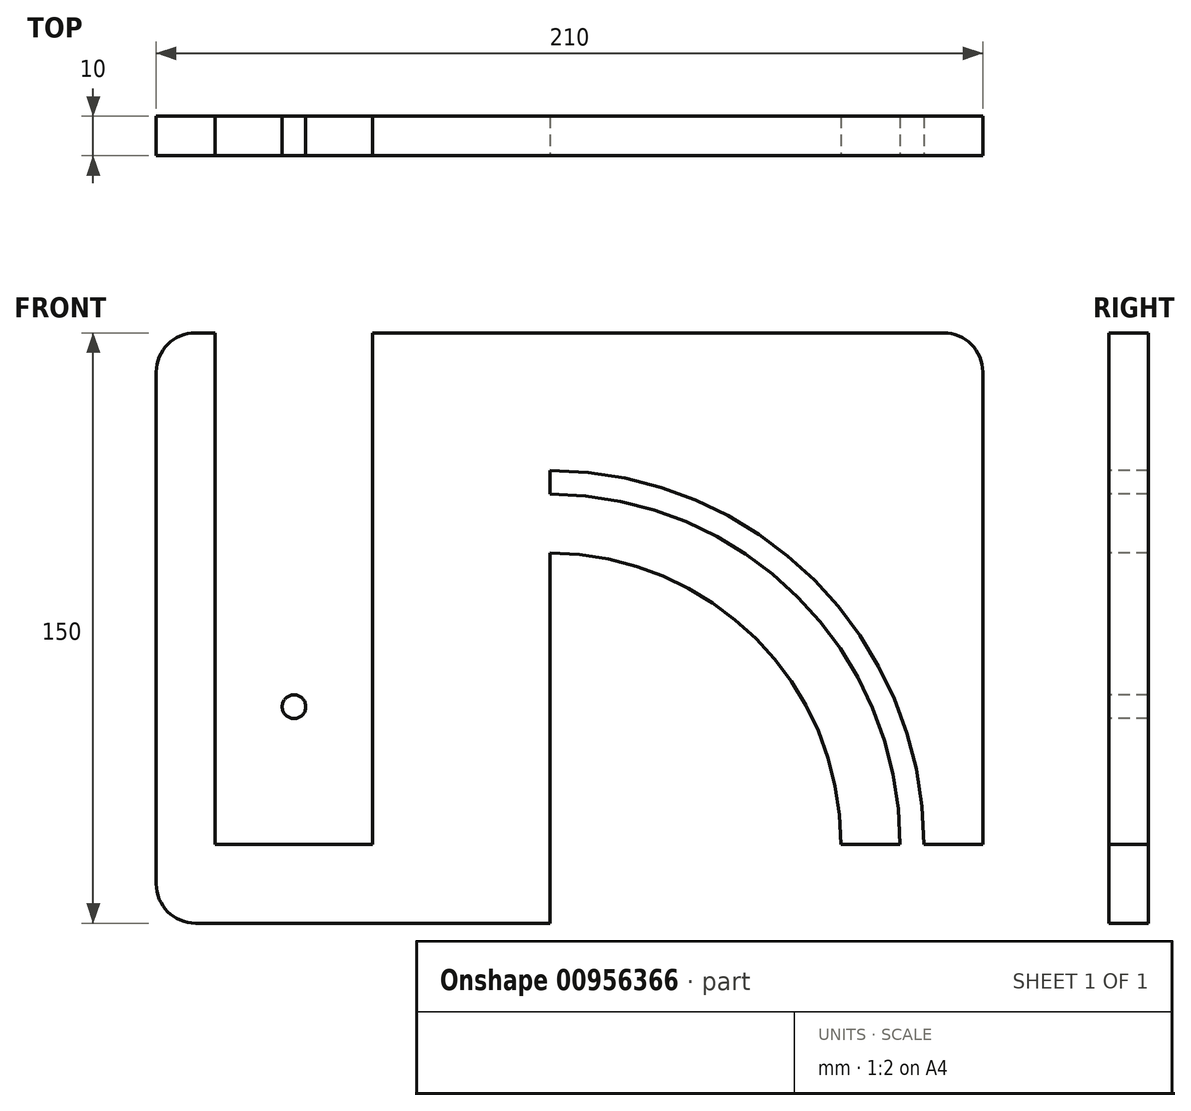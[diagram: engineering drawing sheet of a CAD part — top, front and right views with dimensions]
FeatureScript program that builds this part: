
annotation { "Feature Type Name" : "Feature", "Feature Type Description" : "" }
export const myFeature = defineFeature(function(context is Context, id is Id, definition is map)
    precondition{}
    {
        {
            var Q0;
            Q0=qCreatedBy(makeId("Front.planeOp"),FACE);
            var sketch = newSketch(context, id + "F0", { "sketchPlane" : qUnion([Q0])});
            skLineSegment(sketch, "E0.bottom", {"start": v(-131.27, 125.24) * mm, "end": v(78.73, 125.24) * mm});
            skLineSegment(sketch, "E0.top", {"start": v(-131.27, -24.76) * mm, "end": v(78.73, -24.76) * mm});
            skLineSegment(sketch, "E0.left", {"start": v(-131.27, 125.24) * mm, "end": v(-131.27, -24.76) * mm});
            skLineSegment(sketch, "E0.right", {"start": v(78.73, 125.24) * mm, "end": v(78.73, -24.76) * mm});
            skSolve(sketch);
        }
        {
            var Q0;
            Q0 = qSketchRegion(id + "F0", true);
            extrude(context, id + "F1", {"entities" : qUnion([Q0]), "depth" : 10 * mm, "offsetDistance" : 25.4 * mm});
        }
        {
            var Q0;
            Q0=makeQuery(id+"F1.opExtrude","SWEPT_EDGE",EDGE,{"disambiguationData":[OSD([sQuery(id+"F0.wireOp",EDGE,"E0.bottom"),sQuery(id+"F0.wireOp",EDGE,"E0.left")])]});
            fillet(context, id + "F2", {"entities" : qUnion([Q0]), "radius" : 10 * mm, "tangentPropagation" : true, "allowEdgeOverflow" : false});
        }
        {
            var Q0;
            Q0=makeQuery(id+"F1.opExtrude","SWEPT_EDGE",EDGE,{"disambiguationData":[OSD([sQuery(id+"F0.wireOp",EDGE,"E0.top"),sQuery(id+"F0.wireOp",EDGE,"E0.left")])]});
            fillet(context, id + "F3", {"entities" : qUnion([Q0]), "radius" : 10 * mm, "tangentPropagation" : true, "allowEdgeOverflow" : false});
        }
        {
            var Q0;
            Q0=makeQuery(id+"F1.opExtrude","SWEPT_EDGE",EDGE,{"disambiguationData":[OSD([sQuery(id+"F0.wireOp",EDGE,"E0.top"),sQuery(id+"F0.wireOp",EDGE,"E0.right")])]});
            var Q1;
            Q1=makeQuery(id+"F1.opExtrude","SWEPT_EDGE",EDGE,{"disambiguationData":[OSD([sQuery(id+"F0.wireOp",EDGE,"E0.bottom"),sQuery(id+"F0.wireOp",EDGE,"E0.right")])]});
            fillet(context, id + "F4", {"entities" : qUnion([Q0, Q1]), "radius" : 10 * mm, "tangentPropagation" : true, "allowEdgeOverflow" : false});
        }
        {
            var Q0;
            Q0=makeQuery(id+"F1.opExtrude","CAP_FACE",FACE,{"disambiguationData":[OSD([sQuery(id+"F0.wireOp",EDGE,"E0.bottom"),sQuery(id+"F0.wireOp",EDGE,"E0.top"),sQuery(id+"F0.wireOp",EDGE,"E0.left"),sQuery(id+"F0.wireOp",EDGE,"E0.right")])],"isStart":false});
            var sketch = newSketch(context, id + "F5", { "sketchPlane" : qUnion([Q0])});
            skLineSegment(sketch, "E1", {"start": v(-131.27, -4.76) * mm, "end": v(78.73, -4.76) * mm});
            skCircle(sketch, "E2", {"center": v(-31.27, -4.76) * mm, "radius": 3 * mm});
            skLineSegment(sketch, "E3", {"start": v(-31.27, -24.76) * mm, "end": v(-31.27, 125.24) * mm});
            skArc(sketch, "E4", {"start": v(63.73, -4.76) * mm, "mid": v(35.9, 62.41) * mm, "end": v(-31.27, 90.24) * mm});
            skArc(sketch, "E5", {"start": v(57.73, -4.76) * mm, "mid": v(31.66, 58.17) * mm, "end": v(-31.27, 84.24) * mm});
            skArc(sketch, "E6", {"start": v(42.73, -4.76) * mm, "mid": v(21.06, 47.56) * mm, "end": v(-31.27, 69.24) * mm});
            skArc(sketch, "E7", {"start": v(39.73, -4.76) * mm, "mid": v(18.94, 45.44) * mm, "end": v(-31.27, 66.24) * mm});
            skLineSegment(sketch, "E8", {"start": v(-116.27, -24.76) * mm, "end": v(-116.27, 125.24) * mm});
            skLineSegment(sketch, "E9", {"start": v(-76.27, 125.24) * mm, "end": v(-76.27, -24.76) * mm});
            skLineSegment(sketch, "E10", {"start": v(-96.27, 125.24) * mm, "end": v(-96.27, -24.76) * mm});
            skPoint(sketch, "E11", {"position": v(-96.27, 70.24) * mm});
            skPoint(sketch, "E12", {"position": v(-96.27, 30.24) * mm});
            skCircle(sketch, "E13", {"center": v(-96.27, 70.24) * mm, "radius": 3 * mm});
            skCircle(sketch, "E14", {"center": v(-96.27, 30.24) * mm, "radius": 3 * mm});
            skSolve(sketch);
        }
        {
            var Q0;
            {var subQ0=sQuery(id+"F5.wireOp",EDGE,"E2");var subQ1=sQuery(id+"F5.wireOp",EDGE,"E1");var subQ2=makeQuery(id+"F5.imprint","INTERSECT",VERTEX,{"disambiguationData":[OD(0.0)],"derivedFrom":[subQ1,subQ0]});Q0=makeQuery(id+"F5.imprint","IMPRINT",FACE,{"disambiguationData":[TD([[makeQuery(id+"F5.imprint","IMPRINT",EDGE,{"disambiguationData":[TD([[subQ2,-1.0]])],"derivedFrom":subQ1}),1.0]])]});}
            var Q1;
            {var subQ0=sQuery(id+"F5.wireOp",EDGE,"E2");var subQ1=sQuery(id+"F5.wireOp",EDGE,"E1");var subQ2=makeQuery(id+"F5.imprint","INTERSECT",VERTEX,{"disambiguationData":[OD(0.0)],"derivedFrom":[subQ1,subQ0]});Q1=makeQuery(id+"F5.imprint","IMPRINT",FACE,{"disambiguationData":[TD([[makeQuery(id+"F5.imprint","IMPRINT",EDGE,{"disambiguationData":[TD([[subQ2,-1.0]])],"derivedFrom":subQ1}),-1.0]])]});}
            var Q2;
            {var subQ0=sQuery(id+"F5.wireOp",EDGE,"E3");var subQ1=sQuery(id+"F5.wireOp",EDGE,"E1");var subQ2=makeQuery(id+"F5.imprint","INTERSECT",VERTEX,{"derivedFrom":[subQ1,subQ0]});Q2=makeQuery(id+"F5.imprint","IMPRINT",FACE,{"disambiguationData":[TD([[makeQuery(id+"F5.imprint","IMPRINT",EDGE,{"disambiguationData":[TD([[subQ2,-1.0]])],"derivedFrom":subQ1}),1.0]])]});}
            var Q3;
            {var subQ0=sQuery(id+"F5.wireOp",EDGE,"E3");var subQ1=sQuery(id+"F5.wireOp",EDGE,"E1");var subQ2=makeQuery(id+"F5.imprint","INTERSECT",VERTEX,{"derivedFrom":[subQ1,subQ0]});Q3=makeQuery(id+"F5.imprint","IMPRINT",FACE,{"disambiguationData":[TD([[makeQuery(id+"F5.imprint","IMPRINT",EDGE,{"disambiguationData":[TD([[subQ2,-1.0]])],"derivedFrom":subQ1}),-1.0]])]});}
            var Q4;
            {var subQ0=sQuery(id+"F5.wireOp",EDGE,"E6");Q4=makeQuery(id+"F5.imprint","IMPRINT",FACE,{"disambiguationData":[TD([[makeQuery(id+"F5.imprint","IMPRINT",EDGE,{"derivedFrom":subQ0}),1.0]])]});}
            var Q5;
            {var subQ0=sQuery(id+"F5.wireOp",EDGE,"E4");Q5=makeQuery(id+"F5.imprint","IMPRINT",FACE,{"disambiguationData":[TD([[makeQuery(id+"F5.imprint","IMPRINT",EDGE,{"derivedFrom":subQ0}),1.0]])]});}
            var Q6;
            {var subQ0=sQuery(id+"F5.wireOp",EDGE,"E13");var subQ1=sQuery(id+"F5.wireOp",EDGE,"E10");var subQ2=makeQuery(id+"F5.imprint","INTERSECT",VERTEX,{"disambiguationData":[OD(0.0)],"derivedFrom":[subQ1,subQ0]});Q6=makeQuery(id+"F5.imprint","IMPRINT",FACE,{"disambiguationData":[TD([[makeQuery(id+"F5.imprint","IMPRINT",EDGE,{"disambiguationData":[TD([[subQ2,-1.0]])],"derivedFrom":subQ1}),-1.0]])]});}
            var Q7;
            {var subQ0=sQuery(id+"F5.wireOp",EDGE,"E13");var subQ1=sQuery(id+"F5.wireOp",EDGE,"E10");var subQ2=makeQuery(id+"F5.imprint","INTERSECT",VERTEX,{"disambiguationData":[OD(0.0)],"derivedFrom":[subQ1,subQ0]});Q7=makeQuery(id+"F5.imprint","IMPRINT",FACE,{"disambiguationData":[TD([[makeQuery(id+"F5.imprint","IMPRINT",EDGE,{"disambiguationData":[TD([[subQ2,-1.0]])],"derivedFrom":subQ1}),1.0]])]});}
            var Q8;
            {var subQ0=sQuery(id+"F5.wireOp",EDGE,"E14");var subQ1=sQuery(id+"F5.wireOp",EDGE,"E10");var subQ2=makeQuery(id+"F5.imprint","INTERSECT",VERTEX,{"disambiguationData":[OD(0.0)],"derivedFrom":[subQ1,subQ0]});Q8=makeQuery(id+"F5.imprint","IMPRINT",FACE,{"disambiguationData":[TD([[makeQuery(id+"F5.imprint","IMPRINT",EDGE,{"disambiguationData":[TD([[subQ2,-1.0]])],"derivedFrom":subQ1}),-1.0]])]});}
            var Q9;
            {var subQ0=sQuery(id+"F5.wireOp",EDGE,"E14");var subQ1=sQuery(id+"F5.wireOp",EDGE,"E10");var subQ2=makeQuery(id+"F5.imprint","INTERSECT",VERTEX,{"disambiguationData":[OD(0.0)],"derivedFrom":[subQ1,subQ0]});Q9=makeQuery(id+"F5.imprint","IMPRINT",FACE,{"disambiguationData":[TD([[makeQuery(id+"F5.imprint","IMPRINT",EDGE,{"disambiguationData":[TD([[subQ2,-1.0]])],"derivedFrom":subQ1}),1.0]])]});}
            extrude(context, id + "F6", {"entities" : qUnion([Q0, Q1, Q2, Q3, Q4, Q5, Q6, Q7, Q8, Q9]), "operationType" : NewBodyOperationType.REMOVE, "oppositeDirection" : true, "depth" : 10 * mm, "offsetDistance" : 25.4 * mm});
        }
    });
